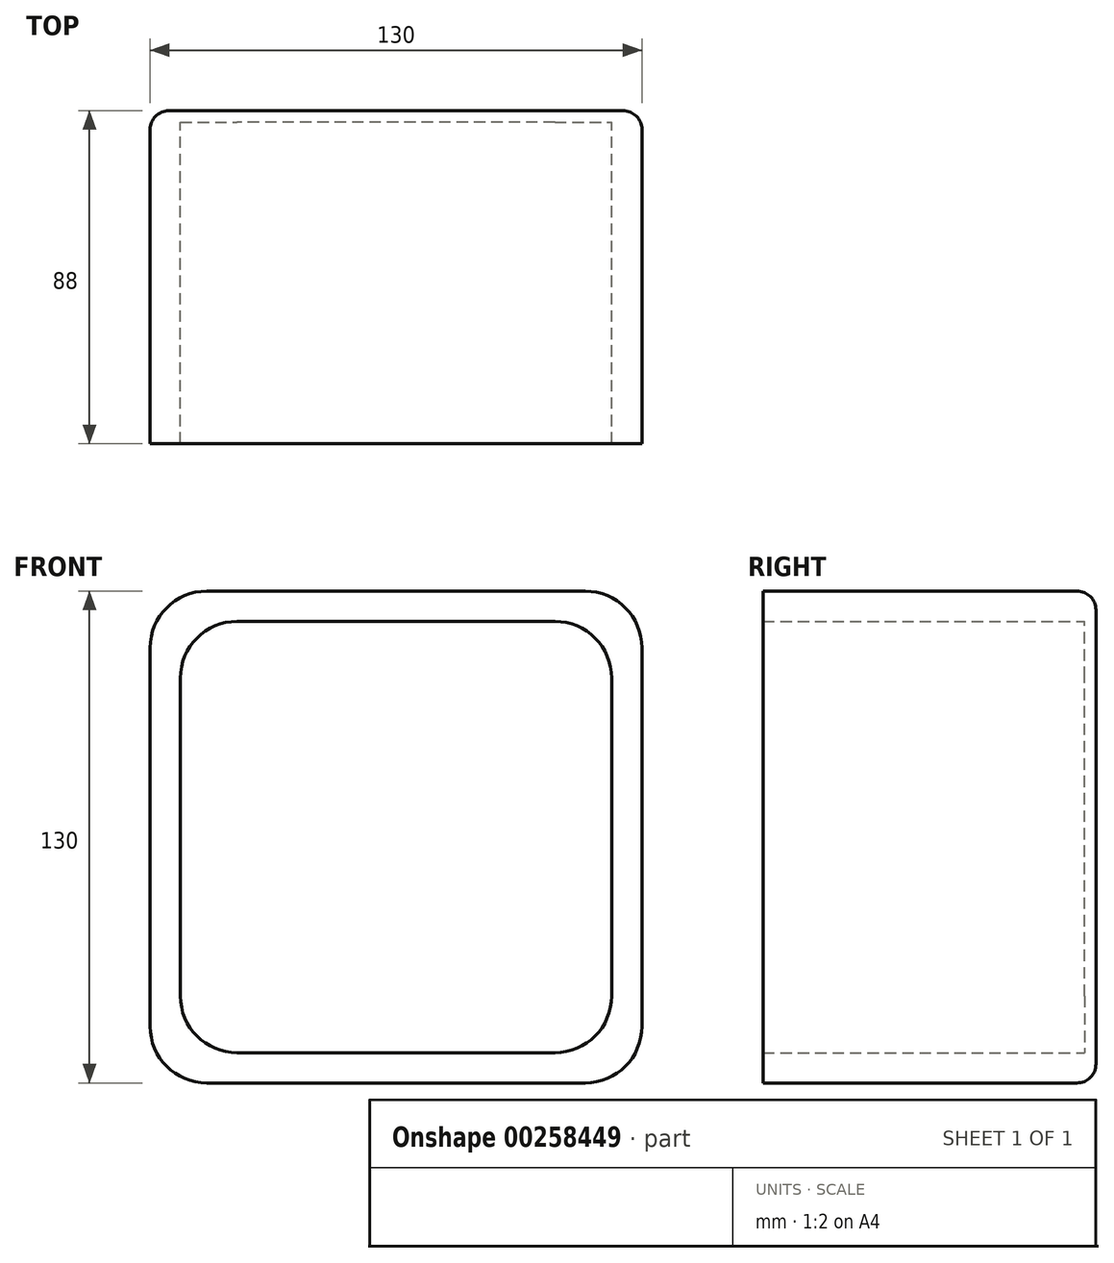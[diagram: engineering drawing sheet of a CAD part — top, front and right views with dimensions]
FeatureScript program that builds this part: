
annotation { "Feature Type Name" : "Feature", "Feature Type Description" : "" }
export const myFeature = defineFeature(function(context is Context, id is Id, definition is map)
    precondition{}
    {
        {
            var Q0;
            Q0=qCreatedBy(makeId("Front.planeOp"),FACE);
            var sketch = newSketch(context, id + "F0", { "sketchPlane" : qUnion([Q0])});
            skLineSegment(sketch, "E0.rect.bottom", {"start": v(65, -65) * mm, "end": v(-65, -65) * mm});
            skLineSegment(sketch, "E0.rect.top", {"start": v(65, 65) * mm, "end": v(-65, 65) * mm});
            skLineSegment(sketch, "E0.rect.left", {"start": v(65, -65) * mm, "end": v(65, 65) * mm});
            skLineSegment(sketch, "E0.rect.right", {"start": v(-65, -65) * mm, "end": v(-65, 65) * mm});
            skPoint(sketch, "E0.rect.middle", {"position": v(0, 0) * mm});
            skLineSegment(sketch, "E1.rect.bottom", {"start": v(57, -57) * mm, "end": v(-57, -57) * mm});
            skLineSegment(sketch, "E1.rect.top", {"start": v(57, 57) * mm, "end": v(-57, 57) * mm});
            skLineSegment(sketch, "E1.rect.left", {"start": v(57, -57) * mm, "end": v(57, 57) * mm});
            skLineSegment(sketch, "E1.rect.right", {"start": v(-57, -57) * mm, "end": v(-57, 57) * mm});
            skLineSegment(sketch, "E2", {"start": v(65, -65) * mm, "end": v(-65, 65) * mm, "construction": true});
            skLineSegment(sketch, "E3", {"start": v(65, 65) * mm, "end": v(-65, -65) * mm, "construction": true});
            skLineSegment(sketch, "E4", {"start": v(65, 0) * mm, "end": v(-65, 0) * mm, "construction": true});
            skLineSegment(sketch, "E5", {"start": v(0, -65) * mm, "end": v(0, 65) * mm, "construction": true});
            skSolve(sketch);
        }
        {
            var Q0;
            Q0=makeQuery(id+"F0.imprint","IMPRINT",FACE,{"disambiguationData":[TD([[makeQuery(id+"F0.imprint","IMPRINT",EDGE,{"derivedFrom":sQuery(id+"F0.wireOp",EDGE,"E0.rect.bottom")}),-1.0]])]});
            extrude(context, id + "F1", {"entities" : qUnion([Q0]), "depth" : 85 * mm});
        }
        {
            var Q0;
            Q0=makeQuery(id+"F1.opExtrude","SWEPT_EDGE",EDGE,{"disambiguationData":[OSD([sQuery(id+"F0.wireOp",EDGE,"E0.rect.top"),sQuery(id+"F0.wireOp",EDGE,"E0.rect.right")])]});
            var Q1;
            Q1=makeQuery(id+"F1.opExtrude","SWEPT_EDGE",EDGE,{"disambiguationData":[OSD([sQuery(id+"F0.wireOp",EDGE,"E1.rect.top"),sQuery(id+"F0.wireOp",EDGE,"E1.rect.right")])]});
            var Q2;
            Q2=makeQuery(id+"F1.opExtrude","SWEPT_EDGE",EDGE,{"disambiguationData":[OSD([sQuery(id+"F0.wireOp",EDGE,"E0.rect.top"),sQuery(id+"F0.wireOp",EDGE,"E0.rect.left")])]});
            var Q3;
            Q3=makeQuery(id+"F1.opExtrude","SWEPT_EDGE",EDGE,{"disambiguationData":[OSD([sQuery(id+"F0.wireOp",EDGE,"E1.rect.top"),sQuery(id+"F0.wireOp",EDGE,"E1.rect.left")])]});
            var Q4;
            Q4=makeQuery(id+"F1.opExtrude","SWEPT_EDGE",EDGE,{"disambiguationData":[OSD([sQuery(id+"F0.wireOp",EDGE,"E0.rect.bottom"),sQuery(id+"F0.wireOp",EDGE,"E0.rect.left")])]});
            var Q5;
            Q5=makeQuery(id+"F1.opExtrude","SWEPT_EDGE",EDGE,{"disambiguationData":[OSD([sQuery(id+"F0.wireOp",EDGE,"E1.rect.bottom"),sQuery(id+"F0.wireOp",EDGE,"E1.rect.left")])]});
            var Q6;
            Q6=makeQuery(id+"F1.opExtrude","SWEPT_EDGE",EDGE,{"disambiguationData":[OSD([sQuery(id+"F0.wireOp",EDGE,"E1.rect.bottom"),sQuery(id+"F0.wireOp",EDGE,"E1.rect.right")])]});
            var Q7;
            Q7=makeQuery(id+"F1.opExtrude","SWEPT_EDGE",EDGE,{"disambiguationData":[OSD([sQuery(id+"F0.wireOp",EDGE,"E0.rect.bottom"),sQuery(id+"F0.wireOp",EDGE,"E0.rect.right")])]});
            fillet(context, id + "F2", {"entities" : qUnion([Q0, Q1, Q2, Q3, Q4, Q5, Q6, Q7]), "radius" : 15 * mm, "tangentPropagation" : true, "allowEdgeOverflow" : false});
        }
        {
            var Q0;
            Q0=makeQuery(id+"F1.opExtrude","CAP_FACE",FACE,{"disambiguationData":[OSD([sQuery(id+"F0.wireOp",EDGE,"E0.rect.bottom"),sQuery(id+"F0.wireOp",EDGE,"E0.rect.top"),sQuery(id+"F0.wireOp",EDGE,"E0.rect.left"),sQuery(id+"F0.wireOp",EDGE,"E0.rect.right"),sQuery(id+"F0.wireOp",EDGE,"E1.rect.bottom"),sQuery(id+"F0.wireOp",EDGE,"E1.rect.top"),sQuery(id+"F0.wireOp",EDGE,"E1.rect.left"),sQuery(id+"F0.wireOp",EDGE,"E1.rect.right")])],"isStart":true});
            var sketch = newSketch(context, id + "F3", { "sketchPlane" : qUnion([Q0])});
            skLineSegment(sketch, "E6.rect.bottom", {"start": v(50, -65) * mm, "end": v(-50, -65) * mm});
            skLineSegment(sketch, "E6.rect.top", {"start": v(50, 65) * mm, "end": v(-50, 65) * mm});
            skLineSegment(sketch, "E6.rect.left", {"start": v(65, -50) * mm, "end": v(65, 50) * mm});
            skLineSegment(sketch, "E6.rect.right", {"start": v(-65, -50) * mm, "end": v(-65, 50) * mm});
            skPoint(sketch, "E6.rect.middle", {"position": v(0, 0) * mm});
            skPoint(sketch, "E7.visualSharp", {"position": v(-65, 65) * mm});
            skArc(sketch, "E7.filletArc", {"start": v(-50, 65) * mm, "mid": v(-60.6, 60.6) * mm, "end": v(-65, 50) * mm});
            skPoint(sketch, "E8.visualSharp", {"position": v(65, 65) * mm});
            skArc(sketch, "E8.filletArc", {"start": v(65, 50) * mm, "mid": v(60.6, 60.6) * mm, "end": v(50, 65) * mm});
            skPoint(sketch, "E9.visualSharp", {"position": v(65, -65) * mm});
            skArc(sketch, "E9.filletArc", {"start": v(50, -65) * mm, "mid": v(60.6, -60.6) * mm, "end": v(65, -50) * mm});
            skPoint(sketch, "E10.visualSharp", {"position": v(-65, -65) * mm});
            skArc(sketch, "E10.filletArc", {"start": v(-65, -50) * mm, "mid": v(-60.6, -60.6) * mm, "end": v(-50, -65) * mm});
            skSolve(sketch);
        }
        {
            var Q0;
            Q0=qSketchRegion(id+"F3",true);
            extrude(context, id + "F4", {"entities" : qUnion([Q0]), "operationType" : NewBodyOperationType.ADD, "depth" : 3 * mm});
        }
        {
            var Q0;
            Q0=makeQuery(id+"F4.opExtrude","CAP_EDGE",EDGE,{"disambiguationData":[OSD([sQuery(id+"F3.wireOp",EDGE,"E10.filletArc")])],"isStart":false});
            fillet(context, id + "F5", {"entities" : qUnion([Q0]), "radius" : 5 * mm, "tangentPropagation" : true, "allowEdgeOverflow" : false});
        }
    });
